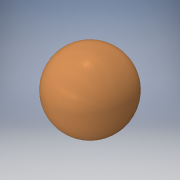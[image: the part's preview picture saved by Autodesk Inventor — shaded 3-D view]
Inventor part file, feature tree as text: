
AUTODESK INVENTOR PART (.ipt)
format: ipt  version: 2016 (Build 200138000, 138)  size: 134,144 bytes
history: native  units: in
note: dims shown in document units (in); Inventor stores cm internally (conversion verified against a paired STEP export)
features: revolve x1, sketch x1
ambient origin geometry x8: Origin, YZ Plane, XZ Plane, XY Plane, X Axis, Y Axis, Z Axis, Center Point
bodies: Solid1 (feature_tree)
feature tree (2):
  revolve  "Revolution1"  [1 undecoded]
  sketch  "Sketch1"  dims[d0=8.0in d1=0.0in d2=90.0deg]
note: 1 required parameter value undecoded (feature->parameter linkage not recoverable at this tier; creation-order binding heuristic only, values carry confidence <= 0.55)
